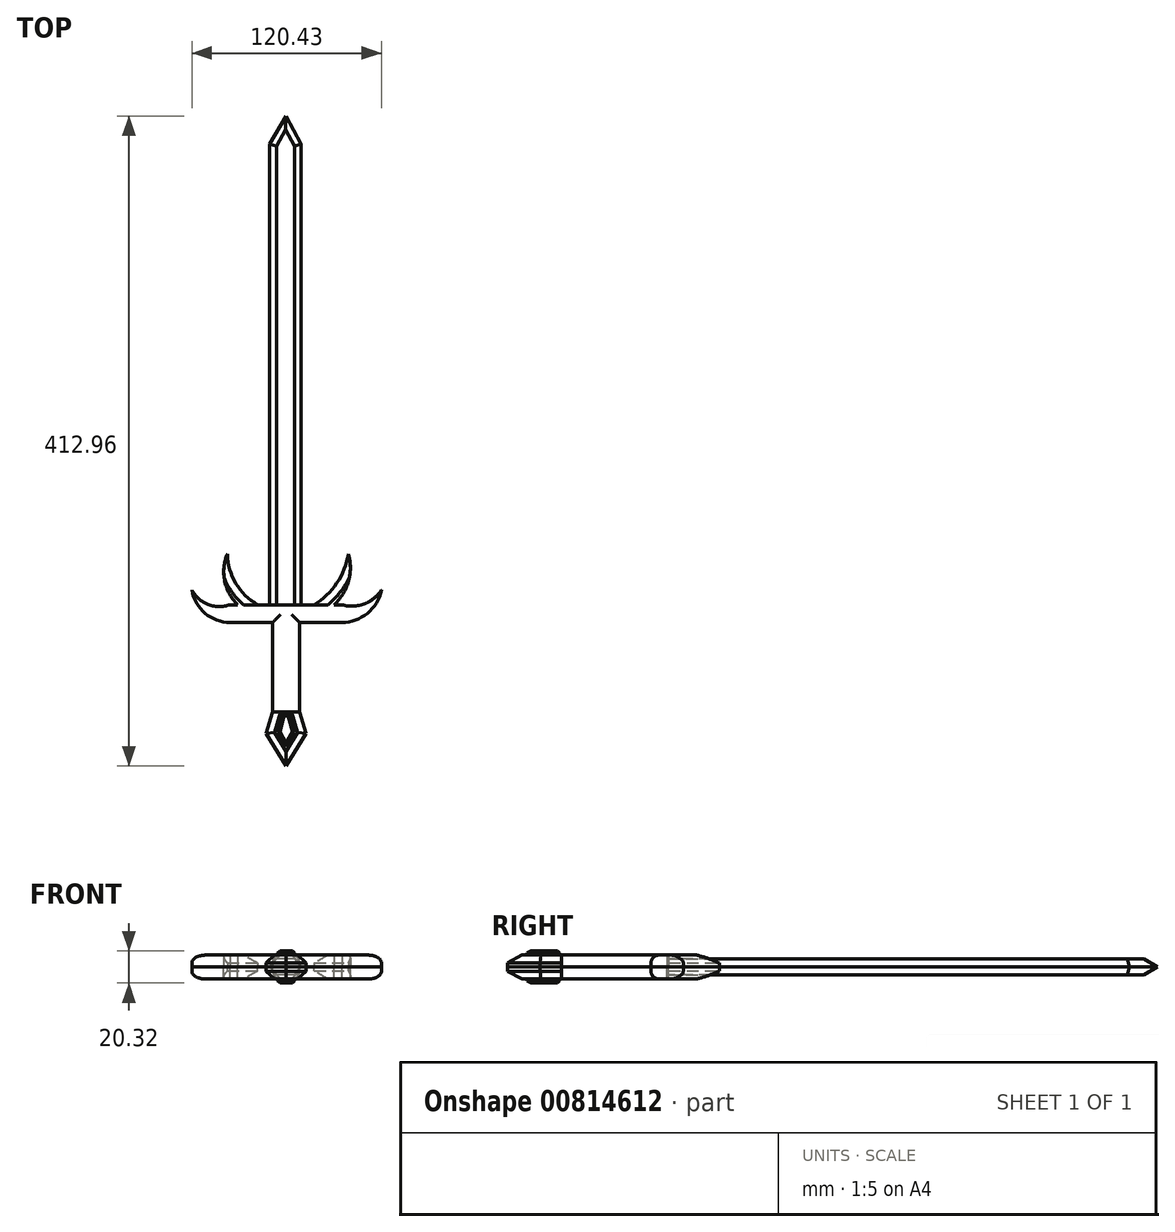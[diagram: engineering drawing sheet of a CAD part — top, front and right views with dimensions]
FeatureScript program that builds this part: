
annotation { "Feature Type Name" : "Feature", "Feature Type Description" : "" }
export const myFeature = defineFeature(function(context is Context, id is Id, definition is map)
    precondition{}
    {
        {
            var Q0;
            Q0=qCreatedBy(makeId("Top.planeOp"),FACE);
            var sketch = newSketch(context, id + "F0", { "sketchPlane" : qUnion([Q0])});
            skLineSegment(sketch, "E0.bottom", {"start": v(-12.77, -26.6) * mm, "end": v(4.23, -26.6) * mm});
            skLineSegment(sketch, "E0.top", {"start": v(-12.77, -94.6) * mm, "end": v(4.23, -94.6) * mm});
            skLineSegment(sketch, "E0.left", {"start": v(-12.77, -26.6) * mm, "end": v(-12.77, -94.6) * mm});
            skLineSegment(sketch, "E0.right", {"start": v(4.23, -26.6) * mm, "end": v(4.23, -94.6) * mm});
            skLineSegment(sketch, "E1.bottom", {"start": v(-39.8, -26.6) * mm, "end": v(31.14, -26.6) * mm});
            skLineSegment(sketch, "E1.top", {"start": v(-39.8, -37.84) * mm, "end": v(31.14, -37.84) * mm});
            skLineSegment(sketch, "E1.left", {"start": v(-39.8, -26.6) * mm, "end": v(-39.8, -37.84) * mm});
            skLineSegment(sketch, "E1.right", {"start": v(31.14, -26.6) * mm, "end": v(31.14, -37.84) * mm});
            skArc(sketch, "E2", {"start": v(-64.15, -17.33) * mm, "mid": v(-55.72, -32.03) * mm, "end": v(-39.8, -37.84) * mm});
            skArc(sketch, "E3", {"start": v(31.14, -37.84) * mm, "mid": v(47.36, -32.06) * mm, "end": v(56.28, -17.33) * mm});
            skArc(sketch, "E4", {"start": v(-64.15, -17.33) * mm, "mid": v(-53.68, -26.43) * mm, "end": v(-39.8, -26.6) * mm});
            skArc(sketch, "E5", {"start": v(31.14, -26.6) * mm, "mid": v(45.2, -26.04) * mm, "end": v(56.28, -17.33) * mm});
            skLineSegment(sketch, "E6", {"start": v(-34.97, -23.72) * mm, "end": v(26.12, -23.72) * mm, "construction": true});
            skArc(sketch, "E7", {"start": v(-41.58, 5.68) * mm, "mid": v(-43.29, -11.48) * mm, "end": v(-34.97, -26.6) * mm});
            skArc(sketch, "E8", {"start": v(-41.58, 5.68) * mm, "mid": v(-36.21, -13.02) * mm, "end": v(-22.28, -26.6) * mm});
            skLineSegment(sketch, "E9", {"start": v(-22.28, -26.6) * mm, "end": v(-34.97, -26.6) * mm});
            skArc(sketch, "E10", {"start": v(26.12, -26.6) * mm, "mid": v(35.33, -11.77) * mm, "end": v(35.3, 5.68) * mm});
            skArc(sketch, "E11", {"start": v(13.48, -26.6) * mm, "mid": v(27.92, -12.85) * mm, "end": v(35.3, 5.68) * mm});
            skLineSegment(sketch, "E12", {"start": v(13.48, -26.6) * mm, "end": v(26.12, -26.6) * mm});
            skLineSegment(sketch, "E13", {"start": v(53.82, 5.68) * mm, "end": v(-69.7, 5.68) * mm, "construction": true});
            skLineSegment(sketch, "E14", {"start": v(-101.97, -69.05) * mm, "end": v(102.54, -69.05) * mm, "construction": true});
            skSolve(sketch);
        }
        {
            var Q0;
            Q0=qSketchRegion(id+"F0",true);
            extrude(context, id + "F1", {"entities" : qUnion([Q0]), "depth" : 7.62 * mm});
        }
        {
            var Q0;
            Q0=makeQuery(id+"F1.opExtrude","CAP_EDGE",EDGE,{"disambiguationData":[OSD([sQuery(id+"F0.wireOp",EDGE,"E0.left")])],"isStart":false});
            var Q1;
            Q1=makeQuery(id+"F1.opExtrude","CAP_EDGE",EDGE,{"disambiguationData":[OSD([sQuery(id+"F0.wireOp",EDGE,"E0.right")])],"isStart":false});
            fillet(context, id + "F2", {"entities" : qUnion([Q0, Q1]), "radius" : 5.08 * mm, "tangentPropagation" : true, "allowEdgeOverflow" : false});
        }
        {
            var Q0;
            Q0=qCreatedBy(makeId("Top.planeOp"),FACE);
            var sketch = newSketch(context, id + "F3", { "sketchPlane" : qUnion([Q0])});
            skLineSegment(sketch, "E15", {"start": v(-12.02, -42.81) * mm, "end": v(-12.02, 28.28) * mm, "construction": true});
            skLineSegment(sketch, "E16", {"start": v(3.2, -43.6) * mm, "end": v(3.2, 29.2) * mm, "construction": true});
            skLineSegment(sketch, "E17", {"start": v(-16.82, -27.15) * mm, "end": v(-16.82, 266.41) * mm});
            skLineSegment(sketch, "E18", {"start": v(-16.82, 266.41) * mm, "end": v(-4.41, 288.3) * mm});
            skLineSegment(sketch, "E19", {"start": v(7.47, 266.41) * mm, "end": v(-4.41, 288.3) * mm});
            skLineSegment(sketch, "E20", {"start": v(7.47, 266.41) * mm, "end": v(7.47, -27.04) * mm});
            skLineSegment(sketch, "E21", {"start": v(7.47, -27.04) * mm, "end": v(-16.82, -27.15) * mm});
            skSolve(sketch);
        }
        {
            var Q0;
            Q0=qSketchRegion(id+"F3",true);
            extrude(context, id + "F4", {"entities" : qUnion([Q0]), "depth" : 5.08 * mm});
        }
        {
            var Q0;
            Q0=makeQuery(id+"F4.opExtrude","CAP_EDGE",EDGE,{"disambiguationData":[OSD([sQuery(id+"F3.wireOp",EDGE,"E17")])],"isStart":false});
            var Q1;
            Q1=makeQuery(id+"F4.opExtrude","CAP_EDGE",EDGE,{"disambiguationData":[OSD([sQuery(id+"F3.wireOp",EDGE,"E20")])],"isStart":false});
            var Q2;
            Q2=makeQuery(id+"F4.opExtrude","CAP_EDGE",EDGE,{"disambiguationData":[OSD([sQuery(id+"F3.wireOp",EDGE,"E18")])],"isStart":false});
            var Q3;
            Q3=makeQuery(id+"F4.opExtrude","CAP_EDGE",EDGE,{"disambiguationData":[OSD([sQuery(id+"F3.wireOp",EDGE,"E19")])],"isStart":false});
            chamfer(context, id + "F5", {"entities" : qUnion([Q0, Q1, Q2, Q3]), "chamferType" : ChamferType.OFFSET_ANGLE, "width" : 7.62 * mm, "oppositeDirection" : false, "angle" : 40 * degree, "tangentPropagation" : true});
        }
        {
            var Q0;
            {var subQ0=sQuery(id+"F0.wireOp",EDGE,"E1.top");Q0=makeQuery(id+"F1.opExtrude","CAP_EDGE",EDGE,{"disambiguationData":[OSD([subQ0]),TDD([makeQuery(id+"F0.imprint","IMPRINT",EDGE,{"disambiguationData":[TD([[makeQuery(id+"F0.imprint","INTERSECT",VERTEX,{"derivedFrom":[sQuery(id+"F0.wireOp",EDGE,"E0.left"),subQ0]}),1.0]])],"derivedFrom":subQ0})])],"isStart":false});}
            var Q1;
            {var subQ0=sQuery(id+"F0.wireOp",EDGE,"E1.top");Q1=makeQuery(id+"F1.opExtrude","CAP_EDGE",EDGE,{"disambiguationData":[OSD([subQ0]),TDD([makeQuery(id+"F0.imprint","IMPRINT",EDGE,{"disambiguationData":[TD([[makeQuery(id+"F0.imprint","INTERSECT",VERTEX,{"derivedFrom":[sQuery(id+"F0.wireOp",EDGE,"E0.right"),subQ0]}),-1.0]])],"derivedFrom":subQ0})])],"isStart":false});}
            fillet(context, id + "F6", {"entities" : qUnion([Q0, Q1]), "radius" : 5.08 * mm, "tangentPropagation" : true, "allowEdgeOverflow" : false});
        }
        {
            var Q0;
            Q0=makeQuery(id+"F1.opExtrude","CAP_EDGE",EDGE,{"disambiguationData":[OSD([sQuery(id+"F0.wireOp",EDGE,"E8")])],"isStart":false});
            var Q1;
            Q1=makeQuery(id+"F1.opExtrude","CAP_EDGE",EDGE,{"disambiguationData":[OSD([sQuery(id+"F0.wireOp",EDGE,"E11")])],"isStart":false});
            chamfer(context, id + "F7", {"entities" : qUnion([Q0, Q1]), "width" : 5.08 * mm, "tangentPropagation" : true});
        }
        {
            var Q0;
            Q0=qCreatedBy(makeId("Top.planeOp"),FACE);
            var sketch = newSketch(context, id + "F8", { "sketchPlane" : qUnion([Q0])});
            skLineSegment(sketch, "E22.top", {"start": v(-12.77, -94.62) * mm, "end": v(4.22, -94.62) * mm});
            skLineSegment(sketch, "E23", {"start": v(-12.77, -94.62) * mm, "end": v(-16.85, -108.25) * mm});
            skLineSegment(sketch, "E24", {"start": v(-16.85, -108.25) * mm, "end": v(-4.27, -129.06) * mm});
            skLineSegment(sketch, "E25", {"start": v(-4.27, -129.06) * mm, "end": v(8.3, -108.25) * mm});
            skLineSegment(sketch, "E26", {"start": v(8.3, -108.25) * mm, "end": v(4.22, -94.62) * mm});
            skLineSegment(sketch, "E27", {"start": v(-36.11, -108.25) * mm, "end": v(28.65, -108.25) * mm, "construction": true});
            skLineSegment(sketch, "E28", {"start": v(-13.9, -93.2) * mm, "end": v(-16.85, -93.2) * mm, "construction": true});
            skLineSegment(sketch, "E29", {"start": v(5.35, -93.46) * mm, "end": v(8.3, -93.46) * mm, "construction": true});
            skPoint(sketch, "E30", {"position": v(-4.27, -94.62) * mm});
            skSolve(sketch);
        }
        {
            var Q0;
            Q0=qSketchRegion(id+"F8",true);
            extrude(context, id + "F9", {"entities" : qUnion([Q0]), "depth" : 7.62 * mm});
        }
        {
            var Q0;
            Q0=makeQuery(id+"F9.opExtrude","CAP_EDGE",EDGE,{"disambiguationData":[OSD([sQuery(id+"F8.wireOp",EDGE,"E24")])],"isStart":false});
            var Q1;
            Q1=makeQuery(id+"F9.opExtrude","CAP_EDGE",EDGE,{"disambiguationData":[OSD([sQuery(id+"F8.wireOp",EDGE,"E25")])],"isStart":false});
            var Q2;
            Q2=makeQuery(id+"F9.opExtrude","CAP_EDGE",EDGE,{"disambiguationData":[OSD([sQuery(id+"F8.wireOp",EDGE,"E23")])],"isStart":false});
            var Q3;
            Q3=makeQuery(id+"F9.opExtrude","CAP_EDGE",EDGE,{"disambiguationData":[OSD([sQuery(id+"F8.wireOp",EDGE,"E26")])],"isStart":false});
            chamfer(context, id + "F10", {"entities" : qUnion([Q0, Q1, Q2, Q3]), "width" : 4.83 * mm, "tangentPropagation" : true});
        }
        {
            var Q0;
            Q0=makeQuery(id+"F9.opExtrude","CAP_FACE",FACE,{"disambiguationData":[OSD([sQuery(id+"F8.wireOp",EDGE,"E22.top"),sQuery(id+"F8.wireOp",EDGE,"E23"),sQuery(id+"F8.wireOp",EDGE,"E24"),sQuery(id+"F8.wireOp",EDGE,"E25"),sQuery(id+"F8.wireOp",EDGE,"E26")])],"isStart":false});
            var sketch = newSketch(context, id + "F11", { "sketchPlane" : qUnion([Q0])});
            skPoint(sketch, "E31.startSnap0", {"position": v(-9.67, -101.1) * mm});
            skLineSegment(sketch, "E32", {"start": v(1.14, -107.59) * mm, "end": v(-4.28, -116.74) * mm});
            skLineSegment(sketch, "E33", {"start": v(-4.28, -116.74) * mm, "end": v(-9.58, -107.59) * mm});
            skLineSegment(sketch, "E34", {"start": v(-9.58, -107.59) * mm, "end": v(-6.67, -96.02) * mm});
            skLineSegment(sketch, "E35", {"start": v(-6.67, -96.02) * mm, "end": v(-1.98, -96.02) * mm});
            skLineSegment(sketch, "E36", {"start": v(-1.98, -96.02) * mm, "end": v(1.14, -107.59) * mm});
            skLineSegment(sketch, "E37", {"start": v(-19.8, -107.59) * mm, "end": v(19.74, -107.59) * mm, "construction": true});
            skSolve(sketch);
        }
        {
            var Q0;
            Q0=qSketchRegion(id+"F11",true);
            extrude(context, id + "F12", {"entities" : qUnion([Q0]), "depth" : 2.54 * mm});
        }
        {
            var Q0;
            Q0=makeQuery(id+"F12.opExtrude","CAP_EDGE",EDGE,{"disambiguationData":[OSD([sQuery(id+"F11.wireOp",EDGE,"E34")])],"isStart":false});
            var Q1;
            Q1=makeQuery(id+"F12.opExtrude","CAP_EDGE",EDGE,{"disambiguationData":[OSD([sQuery(id+"F11.wireOp",EDGE,"E35")])],"isStart":false});
            var Q2;
            Q2=makeQuery(id+"F12.opExtrude","CAP_EDGE",EDGE,{"disambiguationData":[OSD([sQuery(id+"F11.wireOp",EDGE,"E36")])],"isStart":false});
            var Q3;
            Q3=makeQuery(id+"F12.opExtrude","CAP_EDGE",EDGE,{"disambiguationData":[OSD([sQuery(id+"F11.wireOp",EDGE,"E32")])],"isStart":false});
            var Q4;
            Q4=makeQuery(id+"F12.opExtrude","CAP_EDGE",EDGE,{"disambiguationData":[OSD([sQuery(id+"F11.wireOp",EDGE,"E33")])],"isStart":false});
            chamfer(context, id + "F13", {"entities" : qUnion([Q0, Q1, Q2, Q3, Q4]), "width" : 1.27 * mm, "tangentPropagation" : true});
        }
        {
            var Q0;
            Q0=makeQuery(id+"F4.opExtrude","SWEPT_BODY",BODY,{"disambiguationData":[OSD([sQuery(id+"F3.wireOp",EDGE,"E17"),sQuery(id+"F3.wireOp",EDGE,"E18"),sQuery(id+"F3.wireOp",EDGE,"E19"),sQuery(id+"F3.wireOp",EDGE,"E20"),sQuery(id+"F3.wireOp",EDGE,"E21")])]});
            var Q1;
            Q1=makeQuery(id+"F1.opExtrude","SWEPT_BODY",BODY,{"disambiguationData":[OSD([sQuery(id+"F0.wireOp",EDGE,"E0.top"),sQuery(id+"F0.wireOp",EDGE,"E0.left"),sQuery(id+"F0.wireOp",EDGE,"E0.right"),sQuery(id+"F0.wireOp",EDGE,"E1.bottom"),sQuery(id+"F0.wireOp",EDGE,"E1.top"),sQuery(id+"F0.wireOp",EDGE,"E2"),sQuery(id+"F0.wireOp",EDGE,"E3"),sQuery(id+"F0.wireOp",EDGE,"E4"),sQuery(id+"F0.wireOp",EDGE,"E5"),sQuery(id+"F0.wireOp",EDGE,"E7"),sQuery(id+"F0.wireOp",EDGE,"E8"),sQuery(id+"F0.wireOp",EDGE,"E10"),sQuery(id+"F0.wireOp",EDGE,"E11")])]});
            var Q2;
            Q2=makeQuery(id+"F12.opExtrude","SWEPT_BODY",BODY,{"disambiguationData":[OSD([sQuery(id+"F11.wireOp",EDGE,"E32"),sQuery(id+"F11.wireOp",EDGE,"E33"),sQuery(id+"F11.wireOp",EDGE,"E34"),sQuery(id+"F11.wireOp",EDGE,"E35"),sQuery(id+"F11.wireOp",EDGE,"E36")])]});
            var Q3;
            Q3=makeQuery(id+"F9.opExtrude","SWEPT_BODY",BODY,{"disambiguationData":[OSD([sQuery(id+"F8.wireOp",EDGE,"E22.top"),sQuery(id+"F8.wireOp",EDGE,"E23"),sQuery(id+"F8.wireOp",EDGE,"E24"),sQuery(id+"F8.wireOp",EDGE,"E25"),sQuery(id+"F8.wireOp",EDGE,"E26")])]});
            var Q4;
            Q4=qCreatedBy(makeId("Top.planeOp"),FACE);
            mirror(context, id + "F14", {"entities" : qUnion([Q0, Q1, Q2, Q3]), "mirrorPlane" : qUnion([Q4])});
        }
    });
